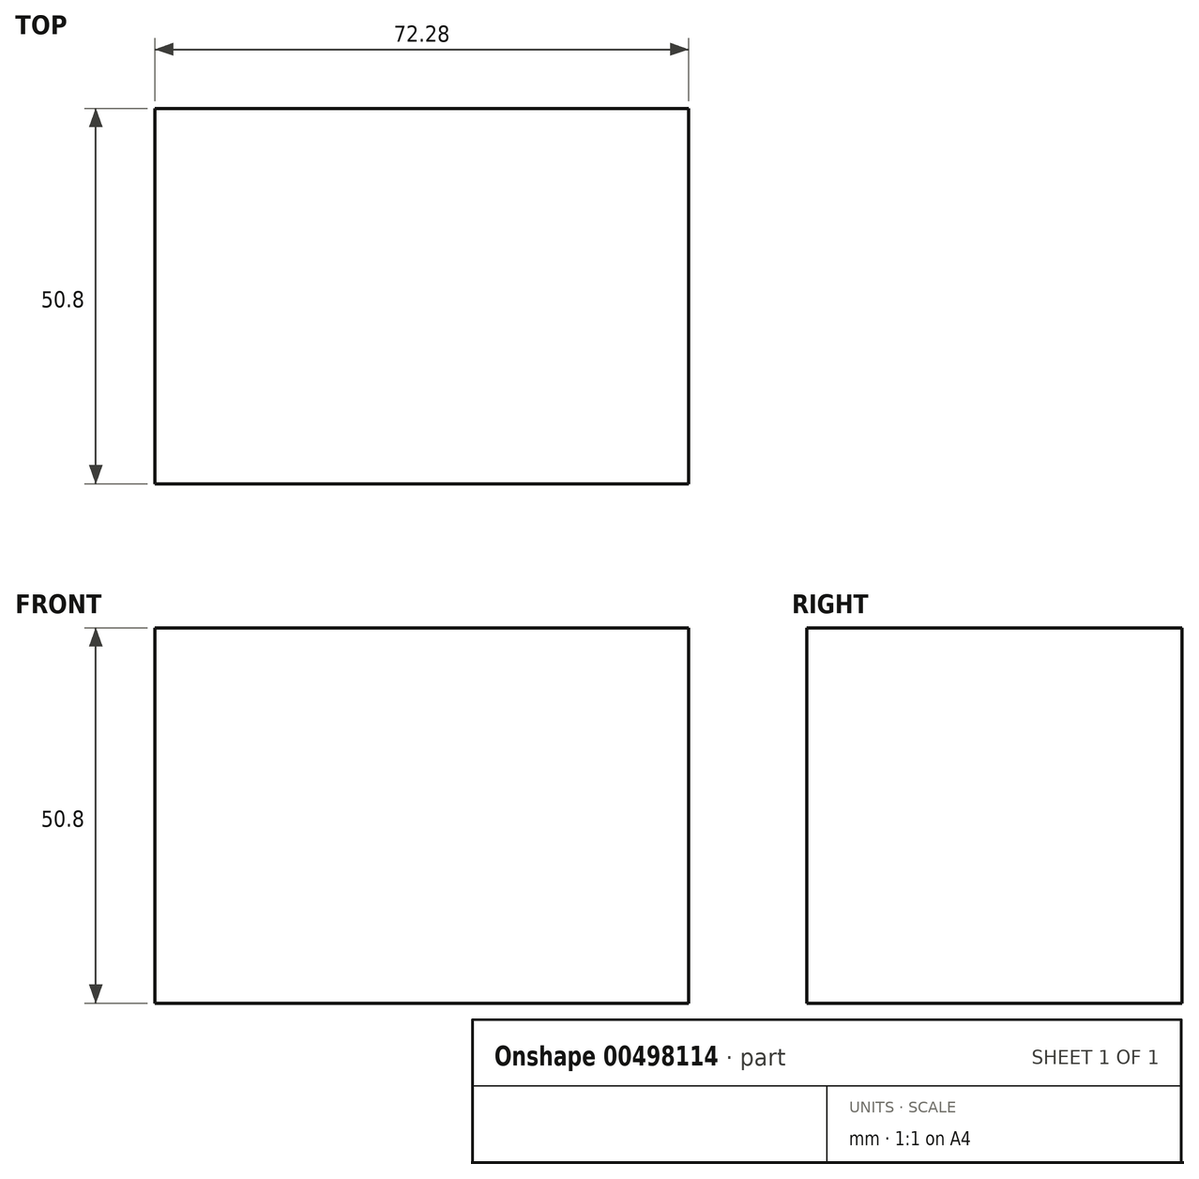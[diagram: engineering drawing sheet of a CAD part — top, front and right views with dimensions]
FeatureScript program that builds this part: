
annotation { "Feature Type Name" : "Feature", "Feature Type Description" : "" }
export const myFeature = defineFeature(function(context is Context, id is Id, definition is map)
    precondition{}
    {
        {
            var Q0;
            Q0=qCreatedBy(makeId("Front.planeOp"),FACE);
            var sketch = newSketch(context, id + "F0", { "sketchPlane" : qUnion([Q0])});
            skLineSegment(sketch, "E0.bottom", {"start": v(0, 0) * mm, "end": v(72.28, 0) * mm});
            skLineSegment(sketch, "E0.top", {"start": v(0, 50.8) * mm, "end": v(72.28, 50.8) * mm});
            skLineSegment(sketch, "E0.left", {"start": v(0, 0) * mm, "end": v(0, 50.8) * mm});
            skLineSegment(sketch, "E0.right", {"start": v(72.28, 0) * mm, "end": v(72.28, 50.8) * mm});
            skSolve(sketch);
        }
        {
            var Q0;
            Q0=makeQuery(id+"F0.imprint","IMPRINT",FACE,{"disambiguationData":[TD([[makeQuery(id+"F0.imprint","IMPRINT",EDGE,{"derivedFrom":sQuery(id+"F0.wireOp",EDGE,"E0.bottom")}),1.0]])]});
            extrude(context, id + "F1", {"entities" : qUnion([Q0]), "depth" : 50.8 * mm});
        }
    });
